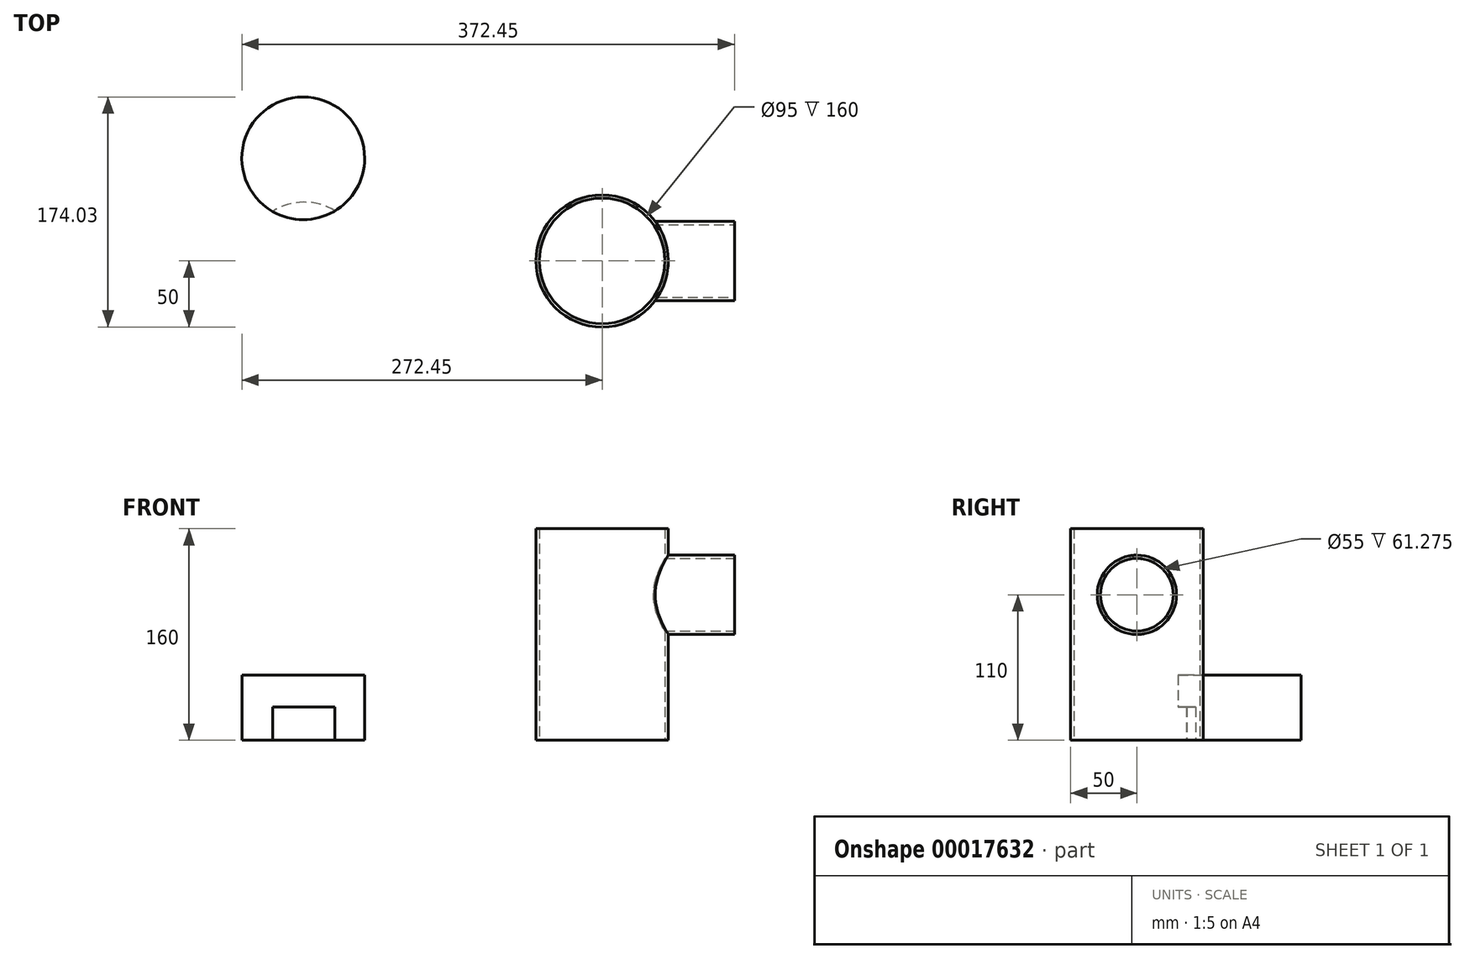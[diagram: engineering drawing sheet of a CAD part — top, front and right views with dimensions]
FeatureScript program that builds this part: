
annotation { "Feature Type Name" : "Feature", "Feature Type Description" : "" }
export const myFeature = defineFeature(function(context is Context, id is Id, definition is map)
    precondition{}
    {
        {
            var Q0;
            Q0=qCreatedBy(makeId("Top.planeOp"),FACE);
            var sketch = newSketch(context, id + "F0", { "sketchPlane" : qUnion([Q0])});
            skCircle(sketch, "E0", {"center": v(0, 0) * mm, "radius": 50 * mm});
            skSolve(sketch);
        }
        {
            var Q0;
            Q0=makeQuery(id+"F0.imprint","IMPRINT",FACE,{"disambiguationData":[TD([[makeQuery(id+"F0.imprint","IMPRINT",EDGE,{"derivedFrom":sQuery(id+"F0.wireOp",EDGE,"E0")}),1.0]])]});
            extrude(context, id + "F1", {"entities" : qUnion([Q0]), "depth" : 160 * mm});
        }
        {
            var Q0;
            Q0=qCreatedBy(makeId("Right.planeOp"),FACE);
            cPlane(context, id + "F2", {"entities" : qUnion([Q0]), "cplaneType" : CPlaneType.OFFSET, "offset" : 100 * mm, "width" : 150 * mm, "height" : 150 * mm});
        }
        {
            var Q0;
            Q0=qCreatedBy(id+"F2.planeOp",FACE);
            var sketch = newSketch(context, id + "F3", { "sketchPlane" : qUnion([Q0])});
            skCircle(sketch, "E1", {"center": v(0, 110) * mm, "radius": 30 * mm});
            skSolve(sketch);
        }
        {
            var Q0;
            Q0=makeQuery(id+"F3.imprint","IMPRINT",FACE,{"disambiguationData":[TD([[makeQuery(id+"F3.imprint","IMPRINT",EDGE,{"derivedFrom":sQuery(id+"F3.wireOp",EDGE,"E1")}),1.0]])]});
            extrude(context, id + "F4", {"entities" : qUnion([Q0]), "operationType" : NewBodyOperationType.ADD, "endBound" : BoundingType.UP_TO_NEXT, "oppositeDirection" : true, "depth" : 82.9 * mm});
        }
        {
            var Q0;
            Q0=makeQuery(id+"F1.opExtrude","CAP_FACE",FACE,{"disambiguationData":[OSD([sQuery(id+"F0.wireOp",EDGE,"E0")])],"isStart":false});
            var Q1;
            Q1=makeQuery(id+"F4.opExtrude","CAP_FACE",FACE,{"disambiguationData":[OSD([sQuery(id+"F3.wireOp",EDGE,"E1")])],"isStart":true});
            var Q2;
            Q2=makeQuery(id+"F1.opExtrude","CAP_FACE",FACE,{"disambiguationData":[OSD([sQuery(id+"F0.wireOp",EDGE,"E0")])],"isStart":true});
            shell(context, id + "F5", {"entities" : qUnion([Q0, Q1, Q2]), "thickness" : 2.5 * mm});
        }
        {
            var Q0;
            Q0=qCreatedBy(makeId("Top.planeOp"),FACE);
            var sketch = newSketch(context, id + "F6", { "sketchPlane" : qUnion([Q0])});
            skCircle(sketch, "E2", {"center": v(-225.26, 0) * mm, "radius": 44.45 * mm});
            skSolve(sketch);
        }
        {
            var Q0;
            Q0=makeQuery(id+"F6.imprint","IMPRINT",FACE,{"disambiguationData":[TD([[makeQuery(id+"F6.imprint","IMPRINT",EDGE,{"derivedFrom":sQuery(id+"F6.wireOp",EDGE,"E2")}),1.0]])]});
            var Q1;
            Q1=sQuery(id+"F6.wireOp",EDGE,"E2");
            extrude(context, id + "F7", {"entities" : qUnion([Q0]), "surfaceEntities" : qUnion([Q1]), "depth" : 25 * mm});
        }
        {
            var Q0;
            Q0=qCreatedBy(makeId("Top.planeOp"),FACE);
            var sketch = newSketch(context, id + "F8", { "sketchPlane" : qUnion([Q0])});
            skCircle(sketch, "E3", {"center": v(-226.03, 77.61) * mm, "radius": 46.42 * mm});
            skSolve(sketch);
        }
        {
            var Q0;
            Q0=makeQuery(id+"F8.imprint","IMPRINT",FACE,{"disambiguationData":[TD([[makeQuery(id+"F8.imprint","IMPRINT",EDGE,{"derivedFrom":sQuery(id+"F8.wireOp",EDGE,"E3")}),1.0]])]});
            extrude(context, id + "F9", {"entities" : qUnion([Q0]), "depth" : 49.23 * mm});
        }
        {
            var Q0;
            Q0=makeQuery(id+"F7.opExtrude","SWEPT_BODY",BODY,{"disambiguationData":[OSD([sQuery(id+"F6.wireOp",EDGE,"E2")])]});
            var Q1;
            Q1=makeQuery(id+"F9.opExtrude","SWEPT_BODY",BODY,{"disambiguationData":[OSD([sQuery(id+"F8.wireOp",EDGE,"E3")])]});
            booleanBodies(context, id + "F10", {"operationType" : BooleanOperationType.SUBTRACTION, "tools" : qUnion([Q0]), "targets" : qUnion([Q1])});
        }
    });
